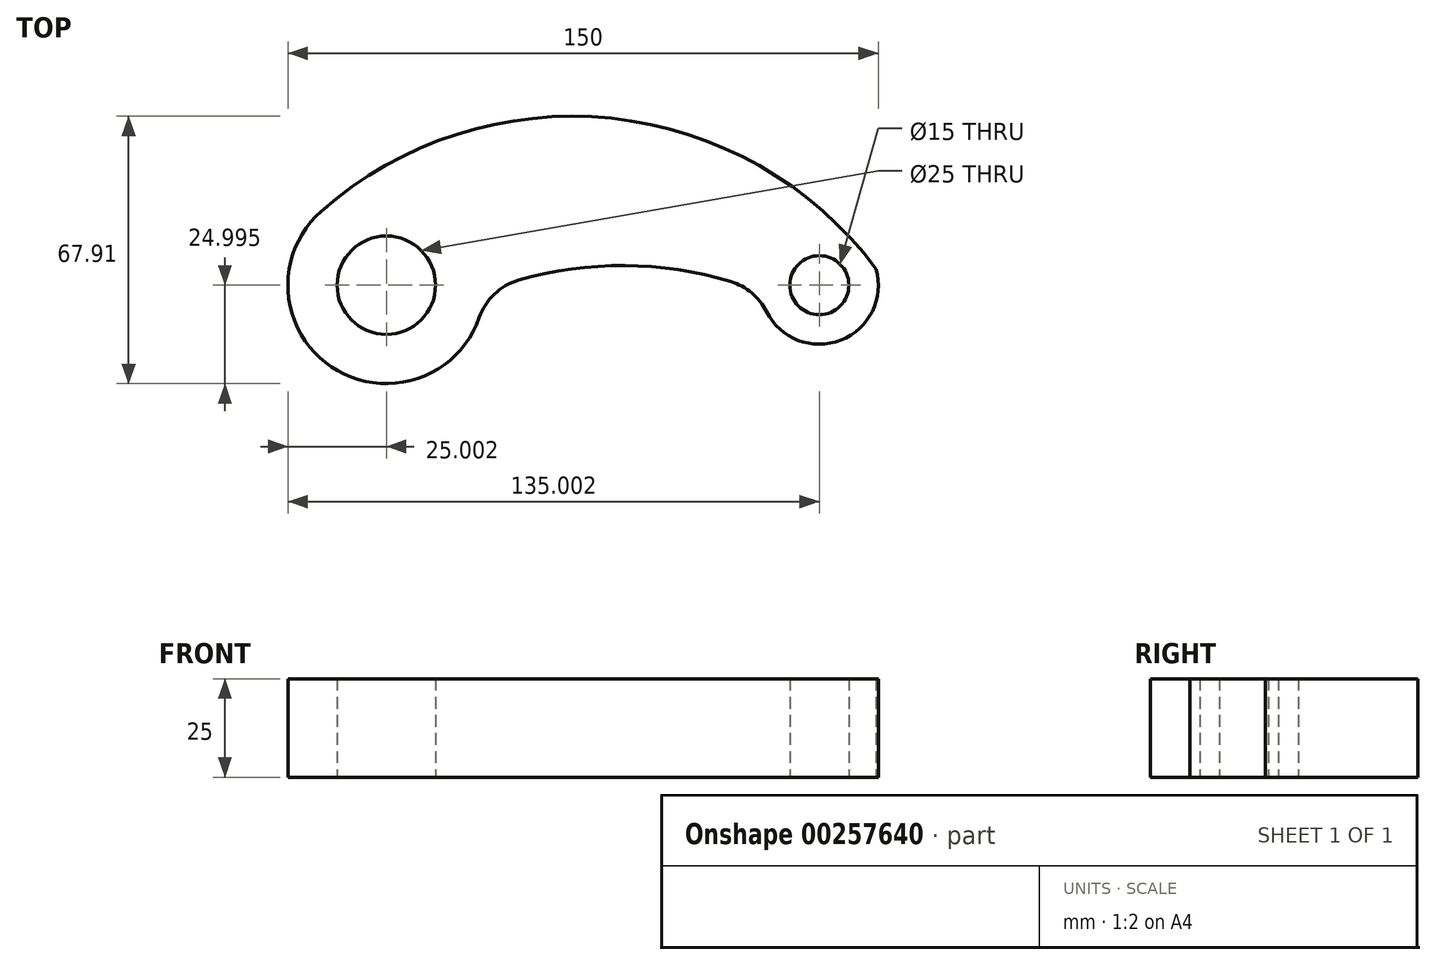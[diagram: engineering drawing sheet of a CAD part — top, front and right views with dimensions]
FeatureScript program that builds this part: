
annotation { "Feature Type Name" : "Feature", "Feature Type Description" : "" }
export const myFeature = defineFeature(function(context is Context, id is Id, definition is map)
    precondition{}
    {
        {
            var Q0;
            Q0=qCreatedBy(makeId("Top.planeOp"),FACE);
            var sketch = newSketch(context, id + "F0", { "sketchPlane" : qUnion([Q0])});
            skLineSegment(sketch, "E0", {"start": v(-57.73, 43.33) * mm, "end": v(-45.23, 43.33) * mm, "construction": true});
            skCircle(sketch, "E1", {"center": v(-57.73, 43.33) * mm, "radius": 12.5 * mm});
            skCircle(sketch, "E2", {"center": v(52.27, 43.33) * mm, "radius": 7.5 * mm});
            skArc(sketch, "E3", {"start": v(-74.24, 62.1) * mm, "mid": v(-71.68, 22.58) * mm, "end": v(-34.12, 35.1) * mm});
            skArc(sketch, "E4", {"start": v(38.86, 36.61) * mm, "mid": v(57.73, 29.35) * mm, "end": v(66.68, 47.48) * mm});
            skLineSegment(sketch, "E5", {"start": v(-57.73, 43.33) * mm, "end": v(-57.73, -46.67) * mm});
            skLineSegment(sketch, "E6", {"start": v(-57.73, -46.67) * mm, "end": v(2.27, -46.67) * mm});
            skArc(sketch, "E7", {"start": v(29.8, 44.25) * mm, "mid": v(2.86, 48.32) * mm, "end": v(-24.12, 44.59) * mm});
            skArc(sketch, "E8", {"start": v(66.68, 47.48) * mm, "mid": v(-0.66, 85.74) * mm, "end": v(-74.38, 61.97) * mm});
            skPoint(sketch, "E8.first.point", {"position": v(-74.38, 61.97) * mm});
            skPoint(sketch, "E8.second.point", {"position": v(66.68, 47.48) * mm});
            skPoint(sketch, "E8.third.point", {"position": v(59.69, -75.8) * mm});
            skLineSegment(sketch, "E9.trimOffspring", {"start": v(-32.73, 43.33) * mm, "end": v(37.27, 43.33) * mm, "construction": true});
            skLineSegment(sketch, "E10.trimOffspring", {"start": v(44.77, 43.33) * mm, "end": v(52.27, 43.33) * mm, "construction": true});
            skArc(sketch, "E11.filletArc", {"start": v(-24.12, 44.59) * mm, "mid": v(-30.27, 41.06) * mm, "end": v(-34.12, 35.1) * mm});
            skArc(sketch, "E12.filletArc", {"start": v(38.86, 36.61) * mm, "mid": v(35.11, 41.37) * mm, "end": v(29.8, 44.25) * mm});
            skSolve(sketch);
        }
        {
            var Q0;
            Q0 = qSketchRegion(id + "F0", true);
            extrude(context, id + "F1", {"entities" : qUnion([Q0]), "depth" : 25 * mm});
        }
    });
